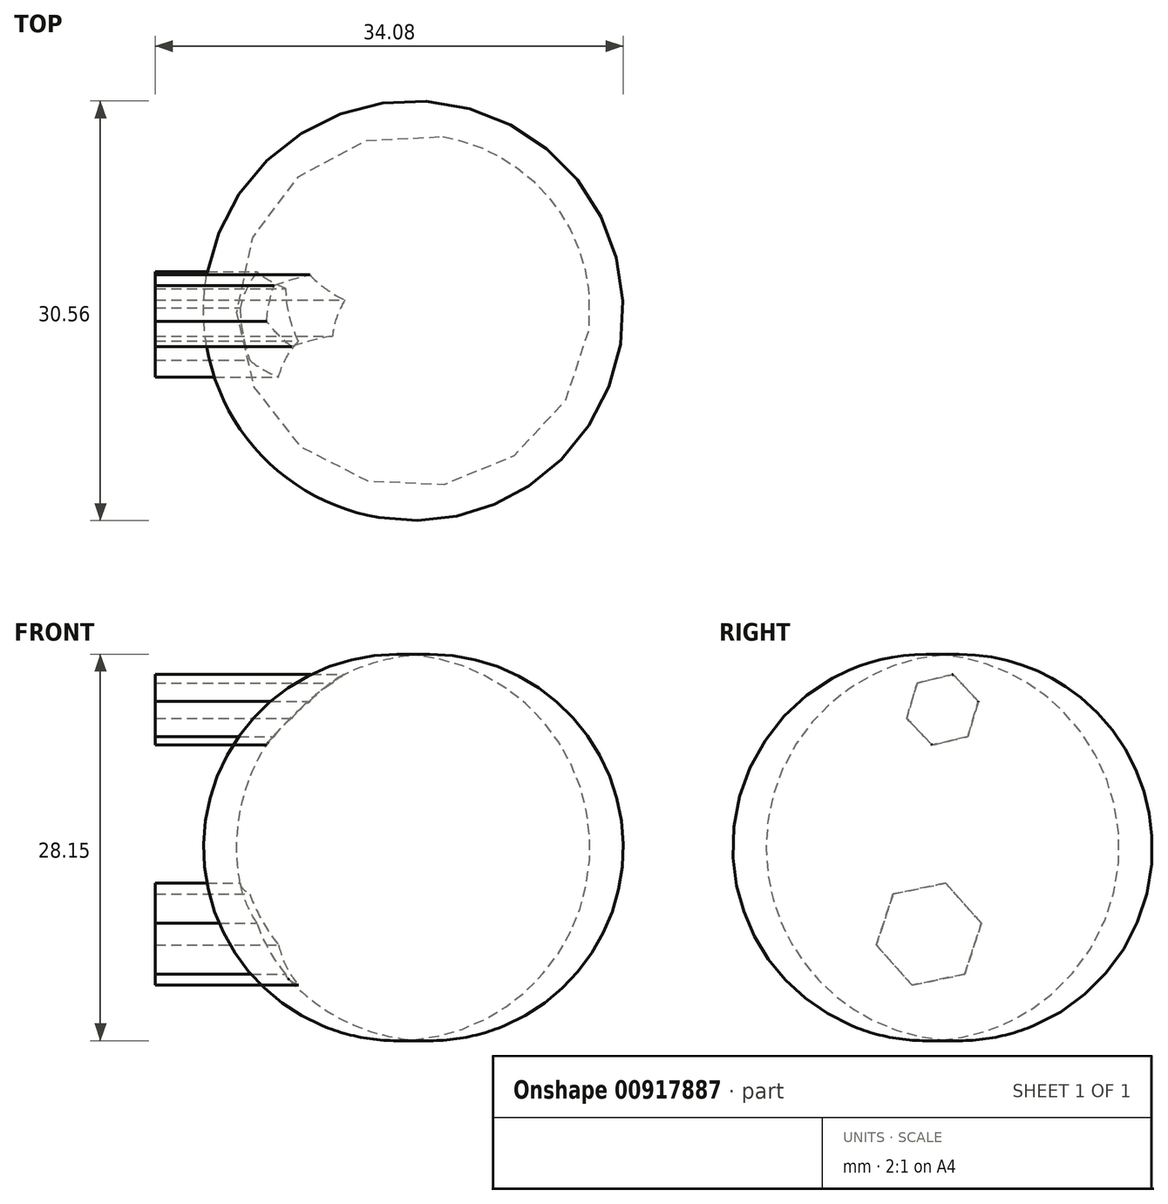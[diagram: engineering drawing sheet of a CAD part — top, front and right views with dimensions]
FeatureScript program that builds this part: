
annotation { "Feature Type Name" : "Feature", "Feature Type Description" : "" }
export const myFeature = defineFeature(function(context is Context, id is Id, definition is map)
    precondition{}
    {
        {
            var Q0;
            Q0=qCreatedBy(makeId("Front.planeOp"),FACE);
            var sketch = newSketch(context, id + "F0", { "sketchPlane" : qUnion([Q0])});
            skLineSegment(sketch, "E0", {"start": v(0, -10.17) * mm, "end": v(0, 17.88) * mm});
            skArc(sketch, "E1", {"start": v(0, -10.17) * mm, "mid": v(12.87, 3.85) * mm, "end": v(0, 17.88) * mm});
            skSolve(sketch);
        }
        {
            var Q0;
            Q0=makeQuery(id+"F0.imprint","IMPRINT",FACE,{"disambiguationData":[TD([[makeQuery(id+"F0.imprint","IMPRINT",EDGE,{"derivedFrom":sQuery(id+"F0.wireOp",EDGE,"E0")}),-1.0]])]});
            var Q1;
            Q1=sQuery(id+"F0.wireOp",EDGE,"E0");
            revolve(context, id + "F1", {"surfaceOperationType" : NewSurfaceOperationType.NEW, "entities" : qUnion([Q0]), "axis" : qUnion([Q1]), "revolveType" : RevolveType.FULL});
        }
        {
            var Q0;
            Q0=qCreatedBy(makeId("Right.planeOp"),FACE);
            var sketch = newSketch(context, id + "F2", { "sketchPlane" : qUnion([Q0])});
            skCircle(sketch, "E2.cCircle", {"center": v(-1, -2.46) * mm, "radius": 3.39 * mm, "construction": true});
            skLineSegment(sketch, "E2.0", {"start": v(-2.22, -6.18) * mm, "end": v(-4.83, -3.26) * mm});
            skLineSegment(sketch, "E2.1", {"start": v(-4.83, -3.26) * mm, "end": v(-3.6, 0.46) * mm});
            skLineSegment(sketch, "E2.2", {"start": v(-3.6, 0.46) * mm, "end": v(0.22, 1.26) * mm});
            skLineSegment(sketch, "E2.3", {"start": v(0.22, 1.26) * mm, "end": v(2.83, -1.66) * mm});
            skLineSegment(sketch, "E2.4", {"start": v(2.83, -1.66) * mm, "end": v(1.61, -5.37) * mm});
            skLineSegment(sketch, "E2.5", {"start": v(1.61, -5.37) * mm, "end": v(-2.22, -6.18) * mm});
            skPoint(sketch, "E2.0.midPoint", {"position": v(-3.52, -4.72) * mm});
            skCircle(sketch, "E3.cCircle", {"center": v(0, 13.89) * mm, "radius": 2.32 * mm, "construction": true});
            skPoint(sketch, "E3.cCircle.perimeterSnap0", {"position": v(-1.7, 0.86) * mm});
            skLineSegment(sketch, "E3.0", {"start": v(-0.77, 11.32) * mm, "end": v(-2.61, 13.27) * mm});
            skLineSegment(sketch, "E3.1", {"start": v(-2.61, 13.27) * mm, "end": v(-1.84, 15.84) * mm});
            skLineSegment(sketch, "E3.2", {"start": v(-1.84, 15.84) * mm, "end": v(0.77, 16.46) * mm});
            skLineSegment(sketch, "E3.3", {"start": v(0.77, 16.46) * mm, "end": v(2.61, 14.5) * mm});
            skLineSegment(sketch, "E3.4", {"start": v(2.61, 14.5) * mm, "end": v(1.84, 11.94) * mm});
            skLineSegment(sketch, "E3.5", {"start": v(1.84, 11.94) * mm, "end": v(-0.77, 11.32) * mm});
            skPoint(sketch, "E3.0.midPoint", {"position": v(-1.7, 12.3) * mm});
            skPoint(sketch, "E3.0.midPoint.positionSnap0", {"position": v(-1.7, 0.86) * mm});
            skSolve(sketch);
        }
        {
            var Q0;
            Q0 = qSketchRegion(id + "F2", true);
            extrude(context, id + "F3", {"entities" : qUnion([Q0]), "operationType" : NewBodyOperationType.ADD, "oppositeDirection" : true, "depth" : 18.8 * mm, "offsetDistance" : 25.4 * mm});
        }
    });
